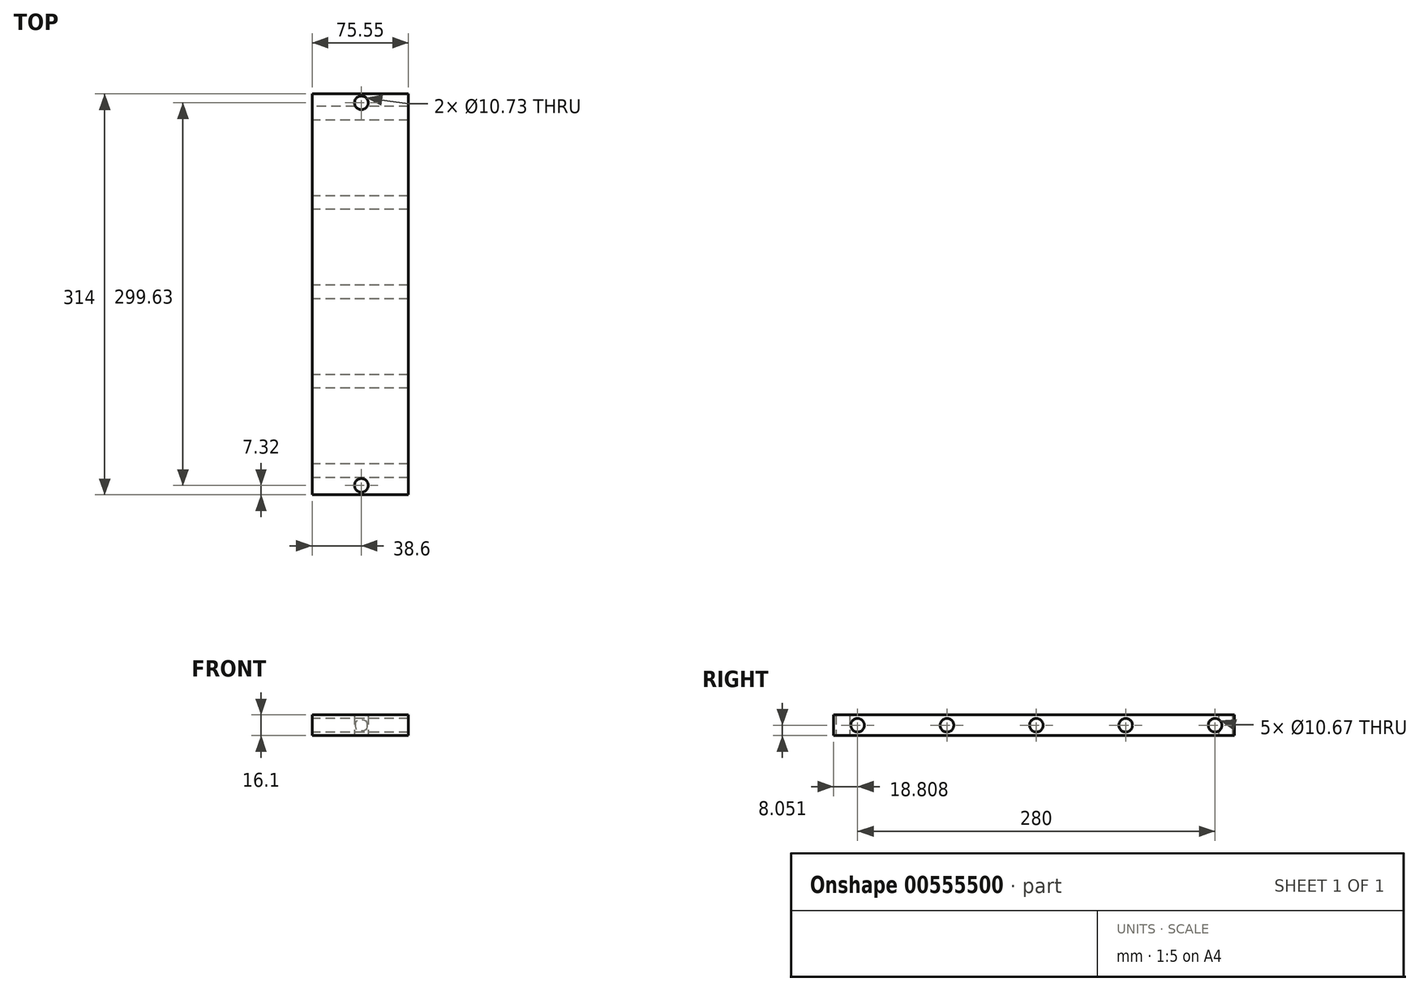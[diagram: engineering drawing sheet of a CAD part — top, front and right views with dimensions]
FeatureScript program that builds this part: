
annotation { "Feature Type Name" : "Feature", "Feature Type Description" : "" }
export const myFeature = defineFeature(function(context is Context, id is Id, definition is map)
    precondition{}
    {
        {
            var Q0;
            Q0=qCreatedBy(makeId("Front.planeOp"),FACE);
            var sketch = newSketch(context, id + "F0", { "sketchPlane" : qUnion([Q0])});
            skLineSegment(sketch, "E0.bottom", {"start": v(-38.6, 30.54) * mm, "end": v(36.95, 30.54) * mm});
            skLineSegment(sketch, "E0.top", {"start": v(-38.6, 14.44) * mm, "end": v(36.95, 14.44) * mm});
            skLineSegment(sketch, "E0.left", {"start": v(-38.6, 30.54) * mm, "end": v(-38.6, 14.44) * mm});
            skLineSegment(sketch, "E0.right", {"start": v(36.95, 30.54) * mm, "end": v(36.95, 14.44) * mm});
            skSolve(sketch);
        }
        {
            var Q0;
            Q0 = qSketchRegion(id + "F0", true);
            extrude(context, id + "F1", {"entities" : qUnion([Q0]), "depth" : 313 * mm, "offsetDistance" : 25 * mm});
        }
        {
            var Q0;
            Q0=makeQuery(id+"F1.opExtrude","SWEPT_FACE",FACE,{"disambiguationData":[OSD([sQuery(id+"F0.wireOp",EDGE,"E0.left")])]});
            var sketch = newSketch(context, id + "F2", { "sketchPlane" : qUnion([Q0])});
            skCircle(sketch, "E1", {"center": v(18.2, 22.5) * mm, "radius": 5.34 * mm});
            skPoint(sketch, "E1.centerSnap0", {"position": v(0, 22.5) * mm});
            skCircle(sketch, "E2", {"center": v(88.2, 22.5) * mm, "radius": 5.34 * mm});
            skCircle(sketch, "E3", {"center": v(158.2, 22.5) * mm, "radius": 5.34 * mm});
            skCircle(sketch, "E4", {"center": v(228.2, 22.5) * mm, "radius": 5.34 * mm});
            skCircle(sketch, "E5", {"center": v(298.2, 22.5) * mm, "radius": 5.34 * mm});
            skSolve(sketch);
        }
        {
            var Q0;
            Q0 = qSketchRegion(id + "F2", true);
            extrude(context, id + "F3", {"entities" : qUnion([Q0]), "operationType" : NewBodyOperationType.REMOVE, "endBound" : BoundingType.THROUGH_ALL, "oppositeDirection" : true, "depth" : 25 * mm, "offsetDistance" : 25 * mm});
        }
        {
            var Q0;
            Q0=makeQuery(id+"F1.opExtrude","CAP_FACE",FACE,{"disambiguationData":[OSD([sQuery(id+"F0.wireOp",EDGE,"E0.bottom"),sQuery(id+"F0.wireOp",EDGE,"E0.top"),sQuery(id+"F0.wireOp",EDGE,"E0.left"),sQuery(id+"F0.wireOp",EDGE,"E0.right")])],"isStart":false});
            extrude(context, id + "F4", {"entities" : qUnion([Q0]), "operationType" : NewBodyOperationType.ADD, "depth" : 4 * mm, "offsetDistance" : 25 * mm});
        }
        {
            var Q0;
            Q0=makeQuery(id+"F1.opExtrude","CAP_FACE",FACE,{"disambiguationData":[OSD([sQuery(id+"F0.wireOp",EDGE,"E0.bottom"),sQuery(id+"F0.wireOp",EDGE,"E0.top"),sQuery(id+"F0.wireOp",EDGE,"E0.left"),sQuery(id+"F0.wireOp",EDGE,"E0.right")])],"isStart":true});
            extrude(context, id + "F5", {"entities" : qUnion([Q0]), "operationType" : NewBodyOperationType.REMOVE, "oppositeDirection" : true, "depth" : 3 * mm, "offsetDistance" : 25 * mm});
        }
        {
            var Q0;
            {var subQ0=sQuery(id+"F0.wireOp",EDGE,"E0.top");Q0=makeQuery(id+"F4.boolean.opBoolean","MERGE",FACE,{"derivedFrom":[makeQuery(id+"F1.opExtrude","SWEPT_FACE",FACE,{"disambiguationData":[OSD([subQ0])]}),makeQuery(id+"F4.opExtrude","SWEPT_FACE",FACE,{"disambiguationData":[OSD([subQ0])]})]});}
            var sketch = newSketch(context, id + "F6", { "sketchPlane" : qUnion([Q0])});
            skCircle(sketch, "E6", {"center": v(0, 309.68) * mm, "radius": 5.36 * mm});
            skSolve(sketch);
        }
        {
            var Q0;
            Q0 = qSketchRegion(id + "F6", true);
            extrude(context, id + "F7", {"entities" : qUnion([Q0]), "operationType" : NewBodyOperationType.REMOVE, "oppositeDirection" : true, "depth" : 25 * mm, "offsetDistance" : 25 * mm});
        }
        {
            var Q0;
            {var subQ0=sQuery(id+"F0.wireOp",EDGE,"E0.top");Q0=makeQuery(id+"F4.boolean.opBoolean","MERGE",FACE,{"derivedFrom":[makeQuery(id+"F1.opExtrude","SWEPT_FACE",FACE,{"disambiguationData":[OSD([subQ0])]}),makeQuery(id+"F4.opExtrude","SWEPT_FACE",FACE,{"disambiguationData":[OSD([subQ0])]})]});}
            var sketch = newSketch(context, id + "F8", { "sketchPlane" : qUnion([Q0])});
            skCircle(sketch, "E7", {"center": v(0, 10.05) * mm, "radius": 5.36 * mm});
            skSolve(sketch);
        }
        {
            var Q0;
            Q0 = qSketchRegion(id + "F8", true);
            extrude(context, id + "F9", {"entities" : qUnion([Q0]), "operationType" : NewBodyOperationType.REMOVE, "oppositeDirection" : true, "depth" : 25 * mm, "offsetDistance" : 25 * mm});
        }
    });
